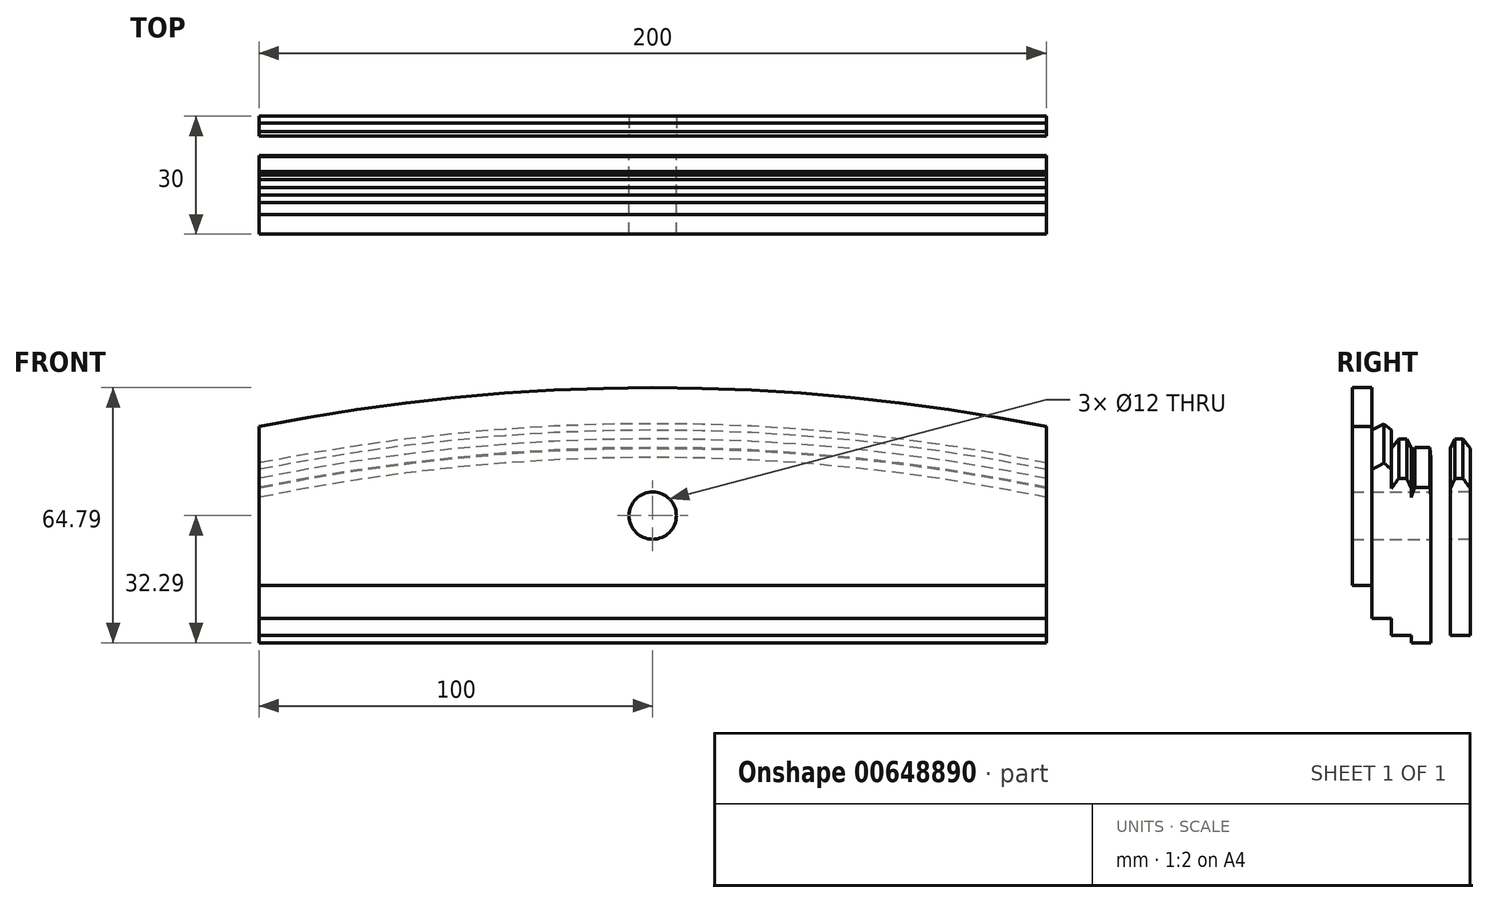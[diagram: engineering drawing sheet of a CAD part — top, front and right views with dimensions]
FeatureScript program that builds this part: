
annotation { "Feature Type Name" : "Feature", "Feature Type Description" : "" }
export const myFeature = defineFeature(function(context is Context, id is Id, definition is map)
    precondition{}
    {
        {
            var Q0;
            Q0=qCreatedBy(makeId("Front.planeOp"),FACE);
            var sketch = newSketch(context, id + "F0", { "sketchPlane" : qUnion([Q0])});
            skCircle(sketch, "E0", {"center": v(0, 0) * mm, "radius": 6 * mm});
            skLineSegment(sketch, "E1.top", {"start": v(-100, -32.3) * mm, "end": v(100, -32.3) * mm});
            skLineSegment(sketch, "E1.left", {"start": v(-100, 7.19) * mm, "end": v(-100, -32.3) * mm});
            skLineSegment(sketch, "E1.right", {"start": v(100, 7.19) * mm, "end": v(100, -32.29) * mm});
            skArc(sketch, "E2", {"start": v(-100, 7.19) * mm, "mid": v(0, 17.3) * mm, "end": v(100, 7.19) * mm});
            skSolve(sketch);
        }
        {
            var Q0;
            Q0=qSketchRegion(id+"F0",true);
            extrude(context, id + "F1", {"entities" : qUnion([Q0]), "depth" : 5 * mm, "offsetDistance" : 25 * mm});
        }
        {
            var Q0;
            Q0=makeQuery(id+"F1.opExtrude","CAP_FACE",FACE,{"disambiguationData":[OSD([sQuery(id+"F0.wireOp",EDGE,"E0"),sQuery(id+"F0.wireOp",EDGE,"E1.top"),sQuery(id+"F0.wireOp",EDGE,"E1.left"),sQuery(id+"F0.wireOp",EDGE,"E1.right"),sQuery(id+"F0.wireOp",EDGE,"E2")])],"isStart":false});
            var sketch = newSketch(context, id + "F2", { "sketchPlane" : qUnion([Q0])});
            skLineSegment(sketch, "E3.bottom", {"start": v(100, -30.49) * mm, "end": v(-100, -30.5) * mm});
            skLineSegment(sketch, "E3.left", {"start": v(100, -30.49) * mm, "end": v(100, 9.45) * mm});
            skLineSegment(sketch, "E3.right", {"start": v(-100, -30.5) * mm, "end": v(-100, 9.45) * mm});
            skPoint(sketch, "E3.middle", {"position": v(0, -5.49) * mm});
            skArc(sketch, "E4.0", {"start": v(-100, 7.19) * mm, "mid": v(0, 17.3) * mm, "end": v(100, 7.19) * mm, "construction": true});
            skArc(sketch, "E5", {"start": v(-100, 9.45) * mm, "mid": v(0, 19.51) * mm, "end": v(100, 9.45) * mm});
            skPoint(sketch, "E6.orphan", {"position": v(-100, 19.5) * mm});
            skPoint(sketch, "E7.orphan", {"position": v(100, 19.51) * mm});
            skCircle(sketch, "E8.0", {"center": v(0, 0) * mm, "radius": 6 * mm});
            skSolve(sketch);
        }
        {
            var Q0;
            Q0=qSketchRegion(id+"F2",true);
            extrude(context, id + "F3", {"entities" : qUnion([Q0]), "depth" : 5 * mm, "offsetDistance" : 25 * mm});
        }
        {
            var Q0;
            Q0=makeQuery(id+"F3.opExtrude","CAP_FACE",FACE,{"disambiguationData":[OSD([sQuery(id+"F2.wireOp",EDGE,"E3.bottom"),sQuery(id+"F2.wireOp",EDGE,"E3.left"),sQuery(id+"F2.wireOp",EDGE,"E3.right"),sQuery(id+"F2.wireOp",EDGE,"E5"),sQuery(id+"F2.wireOp",EDGE,"E8.0")])],"isStart":false});
            var sketch = newSketch(context, id + "F4", { "sketchPlane" : qUnion([Q0])});
            skLineSegment(sketch, "E9.bottom", {"start": v(100, -26.09) * mm, "end": v(-100, -26.1) * mm});
            skLineSegment(sketch, "E9.left", {"start": v(100, -26.09) * mm, "end": v(100, 14.25) * mm});
            skLineSegment(sketch, "E9.right", {"start": v(-100, -26.1) * mm, "end": v(-100, 14.25) * mm});
            skPoint(sketch, "E9.middle", {"position": v(0, -0.94) * mm});
            skArc(sketch, "E10.0", {"start": v(-100, 9.45) * mm, "mid": v(0, 19.51) * mm, "end": v(100, 9.45) * mm, "construction": true});
            skArc(sketch, "E11", {"start": v(-100, 14.25) * mm, "mid": v(0, 24.2) * mm, "end": v(100, 14.25) * mm});
            skCircle(sketch, "E12.0", {"center": v(0, 0) * mm, "radius": 6 * mm});
            skPoint(sketch, "E13.orphan", {"position": v(-100, 24.2) * mm});
            skPoint(sketch, "E14.orphan", {"position": v(100, 24.21) * mm});
            skSolve(sketch);
        }
        {
            var Q0;
            Q0=qSketchRegion(id+"F4",true);
            extrude(context, id + "F5", {"entities" : qUnion([Q0]), "depth" : 5 * mm, "offsetDistance" : 25 * mm});
        }
        {
            var Q0;
            Q0=makeQuery(id+"F5.opExtrude","CAP_FACE",FACE,{"disambiguationData":[OSD([sQuery(id+"F4.wireOp",EDGE,"E9.bottom"),sQuery(id+"F4.wireOp",EDGE,"E9.left"),sQuery(id+"F4.wireOp",EDGE,"E9.right"),sQuery(id+"F4.wireOp",EDGE,"E11"),sQuery(id+"F4.wireOp",EDGE,"E12.0")])],"isStart":false});
            var sketch = newSketch(context, id + "F6", { "sketchPlane" : qUnion([Q0])});
            skLineSegment(sketch, "E15.bottom", {"start": v(100, -17.79) * mm, "end": v(-100, -17.8) * mm});
            skLineSegment(sketch, "E15.left", {"start": v(100, -17.79) * mm, "end": v(100, 22.7) * mm});
            skLineSegment(sketch, "E15.right", {"start": v(-100, -17.8) * mm, "end": v(-100, 22.7) * mm});
            skPoint(sketch, "E15.middle", {"position": v(0, 7.36) * mm});
            skArc(sketch, "E16.0", {"start": v(-100, 14.25) * mm, "mid": v(0, 24.2) * mm, "end": v(100, 14.25) * mm, "construction": true});
            skArc(sketch, "E17", {"start": v(-100, 22.7) * mm, "mid": v(0, 32.5) * mm, "end": v(100, 22.7) * mm});
            skPoint(sketch, "E18.orphan", {"position": v(-100, 32.5) * mm});
            skPoint(sketch, "E19.orphan", {"position": v(100, 32.5) * mm});
            skCircle(sketch, "E20.0", {"center": v(0, 0) * mm, "radius": 6 * mm});
            skSolve(sketch);
        }
        {
            var Q0;
            Q0=qSketchRegion(id+"F6",true);
            extrude(context, id + "F7", {"entities" : qUnion([Q0]), "depth" : 5 * mm, "offsetDistance" : 25 * mm});
        }
        {
            var Q0;
            Q0=makeQuery(id+"F1.opExtrude","CAP_EDGE",EDGE,{"disambiguationData":[OSD([sQuery(id+"F0.wireOp",EDGE,"E2")])],"isStart":true});
            chamfer(context, id + "F8", {"entities" : qUnion([Q0]), "chamferType" : ChamferType.OFFSET_ANGLE, "width" : 2.5 * mm, "oppositeDirection" : true, "angle" : 4.7 * degree, "tangentPropagation" : true});
        }
        {
            var Q0;
            Q0=makeQuery(id+"F3.opExtrude","CAP_EDGE",EDGE,{"disambiguationData":[OSD([sQuery(id+"F2.wireOp",EDGE,"E5")])],"isStart":true});
            chamfer(context, id + "F9", {"entities" : qUnion([Q0]), "chamferType" : ChamferType.OFFSET_ANGLE, "width" : 2.5 * mm, "oppositeDirection" : true, "angle" : 24.7 * degree, "tangentPropagation" : true});
        }
        {
            var Q0;
            Q0=makeQuery(id+"F5.opExtrude","CAP_EDGE",EDGE,{"disambiguationData":[OSD([sQuery(id+"F4.wireOp",EDGE,"E11")])],"isStart":true});
            chamfer(context, id + "F10", {"entities" : qUnion([Q0]), "chamferType" : ChamferType.OFFSET_ANGLE, "width" : 2.5 * mm, "oppositeDirection" : true, "angle" : 49.1 * degree, "tangentPropagation" : true});
        }
        {
            var Q0;
            Q0=makeQuery(id+"F1.opExtrude","CAP_EDGE",EDGE,{"disambiguationData":[OSD([sQuery(id+"F0.wireOp",EDGE,"E2")])],"isStart":false});
            chamfer(context, id + "F11", {"entities" : qUnion([Q0]), "chamferType" : ChamferType.OFFSET_ANGLE, "width" : 2.5 * mm, "oppositeDirection" : false, "angle" : 20 * degree, "tangentPropagation" : true});
        }
        {
            var Q0;
            Q0=makeQuery(id+"F3.opExtrude","CAP_EDGE",EDGE,{"disambiguationData":[OSD([sQuery(id+"F2.wireOp",EDGE,"E5")])],"isStart":false});
            chamfer(context, id + "F12", {"entities" : qUnion([Q0]), "chamferType" : ChamferType.OFFSET_ANGLE, "width" : 2.5 * mm, "oppositeDirection" : false, "angle" : 35.9 * degree, "tangentPropagation" : true});
        }
        {
            var Q0;
            Q0=makeQuery(id+"F5.opExtrude","CAP_EDGE",EDGE,{"disambiguationData":[OSD([sQuery(id+"F4.wireOp",EDGE,"E11")])],"isStart":false});
            chamfer(context, id + "F13", {"entities" : qUnion([Q0]), "chamferType" : ChamferType.OFFSET_ANGLE, "width" : 2.5 * mm, "oppositeDirection" : false, "angle" : 62.1 * degree, "tangentPropagation" : true});
        }
        {
            var Q0;
            Q0=makeQuery(id+"F3.opExtrude","SWEPT_BODY",BODY,{"disambiguationData":[OSD([sQuery(id+"F2.wireOp",EDGE,"E3.bottom"),sQuery(id+"F2.wireOp",EDGE,"E3.left"),sQuery(id+"F2.wireOp",EDGE,"E3.right"),sQuery(id+"F2.wireOp",EDGE,"E5"),sQuery(id+"F2.wireOp",EDGE,"E8.0")])]});
            var Q1;
            Q1=qCreatedBy(makeId("Front.planeOp"),FACE);
            mirror(context, id + "F14", {"operationType" : NewBodyOperationType.ADD, "entities" : qUnion([Q0]), "mirrorPlane" : qUnion([Q1])});
        }
    });
